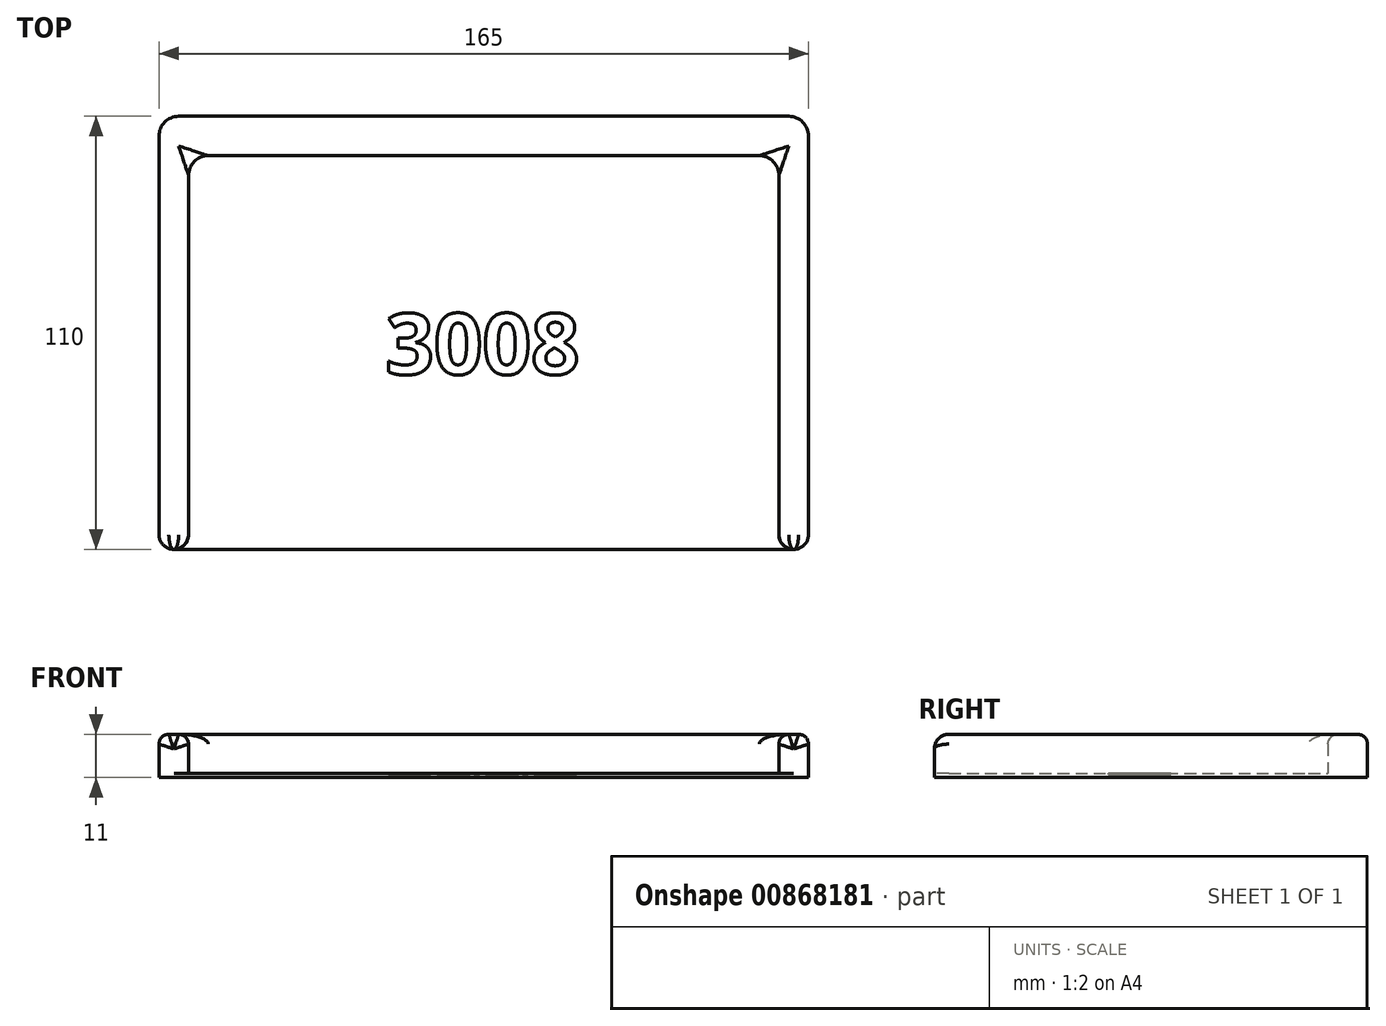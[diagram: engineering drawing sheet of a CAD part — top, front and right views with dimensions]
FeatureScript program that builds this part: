
annotation { "Feature Type Name" : "Feature", "Feature Type Description" : "" }
export const myFeature = defineFeature(function(context is Context, id is Id, definition is map)
    precondition{}
    {
        {
            var Q0;
            Q0=qCreatedBy(makeId("Top.planeOp"),FACE);
            var sketch = newSketch(context, id + "F0", { "sketchPlane" : qUnion([Q0])});
            skLineSegment(sketch, "E0.bottom", {"start": v(0, 0) * mm, "end": v(165, 0) * mm});
            skLineSegment(sketch, "E0.top", {"start": v(0, 110) * mm, "end": v(165, 110) * mm});
            skLineSegment(sketch, "E0.left", {"start": v(0, 0) * mm, "end": v(0, 110) * mm});
            skLineSegment(sketch, "E0.right", {"start": v(165, 0) * mm, "end": v(165, 110) * mm});
            skSolve(sketch);
        }
        {
            var Q0;
            Q0 = qSketchRegion(id + "F0", true);
            extrude(context, id + "F1", {"entities" : qUnion([Q0]), "depth" : 1 * mm, "offsetDistance" : 25 * mm});
        }
        {
            var Q0;
            Q0=makeQuery(id+"F1.opExtrude","CAP_FACE",FACE,{"disambiguationData":[OSD([sQuery(id+"F0.wireOp",EDGE,"E0.bottom"),sQuery(id+"F0.wireOp",EDGE,"E0.top"),sQuery(id+"F0.wireOp",EDGE,"E0.left"),sQuery(id+"F0.wireOp",EDGE,"E0.right")])],"isStart":false});
            var sketch = newSketch(context, id + "F2", { "sketchPlane" : qUnion([Q0])});
            skLineSegment(sketch, "E1", {"start": v(0, 0) * mm, "end": v(0, 110) * mm});
            skLineSegment(sketch, "E2", {"start": v(0, 110) * mm, "end": v(165, 110) * mm});
            skLineSegment(sketch, "E3", {"start": v(165, 110) * mm, "end": v(165, 0) * mm});
            skLineSegment(sketch, "E4", {"start": v(165, 0) * mm, "end": v(157.5, 0) * mm});
            skLineSegment(sketch, "E5", {"start": v(157.5, 0) * mm, "end": v(157.5, 100) * mm});
            skLineSegment(sketch, "E6", {"start": v(157.5, 100) * mm, "end": v(7.5, 100) * mm});
            skLineSegment(sketch, "E7", {"start": v(7.5, 100) * mm, "end": v(7.5, 0) * mm});
            skLineSegment(sketch, "E8", {"start": v(7.5, 0) * mm, "end": v(0, 0) * mm});
            skSolve(sketch);
        }
        {
            var Q0;
            Q0 = qSketchRegion(id + "F2", true);
            extrude(context, id + "F3", {"entities" : qUnion([Q0]), "operationType" : NewBodyOperationType.ADD, "depth" : 10 * mm, "offsetDistance" : 25 * mm});
        }
        {
            var Q0;
            Q0=makeQuery(id+"F3.opExtrude","CAP_EDGE",EDGE,{"disambiguationData":[OSD([sQuery(id+"F2.wireOp",EDGE,"E7")])],"isStart":false});
            var Q1;
            Q1=makeQuery(id+"F3.opExtrude","CAP_EDGE",EDGE,{"disambiguationData":[OSD([sQuery(id+"F2.wireOp",EDGE,"E6")])],"isStart":false});
            var Q2;
            Q2=makeQuery(id+"F3.opExtrude","CAP_EDGE",EDGE,{"disambiguationData":[OSD([sQuery(id+"F2.wireOp",EDGE,"E5")])],"isStart":false});
            var Q3;
            Q3=makeQuery(id+"F3.opExtrude","CAP_EDGE",EDGE,{"disambiguationData":[OSD([sQuery(id+"F2.wireOp",EDGE,"E1")])],"isStart":false});
            var Q4;
            Q4=makeQuery(id+"F3.opExtrude","CAP_EDGE",EDGE,{"disambiguationData":[OSD([sQuery(id+"F2.wireOp",EDGE,"E2")])],"isStart":false});
            var Q5;
            Q5=makeQuery(id+"F3.opExtrude","CAP_EDGE",EDGE,{"disambiguationData":[OSD([sQuery(id+"F2.wireOp",EDGE,"E3")])],"isStart":false});
            fillet(context, id + "F4", {"entities" : qUnion([Q0, Q1, Q2, Q3, Q4, Q5]), "radius" : 2.5 * mm, "tangentPropagation" : true, "allowEdgeOverflow" : false});
        }
        {
            var Q0;
            Q0=makeQuery(id+"F1.opExtrude","CAP_FACE",FACE,{"disambiguationData":[OSD([sQuery(id+"F0.wireOp",EDGE,"E0.bottom"),sQuery(id+"F0.wireOp",EDGE,"E0.top"),sQuery(id+"F0.wireOp",EDGE,"E0.left"),sQuery(id+"F0.wireOp",EDGE,"E0.right")])],"isStart":false});
            var sketch = newSketch(context, id + "F5", { "sketchPlane" : qUnion([Q0])});
            skText(sketch, "E9", { "text": "3008", "fontName": "OpenSans-Bold.ttf"});
            const initialGuessF5  = {"E9": [0.0575, 0.04444, 1, 0, 0.01556]};
            skSetInitialGuess(sketch, initialGuessF5);
            skSolve(sketch);
        }
        {
            var Q0;
            Q0 = qSketchRegion(id + "F5", true);
            extrude(context, id + "F6", {"entities" : qUnion([Q0]), "operationType" : NewBodyOperationType.REMOVE, "oppositeDirection" : true, "depth" : .2 * mm, "offsetDistance" : 25 * mm});
        }
        {
            var Q0;
            Q0=makeQuery(id+"F3.opExtrude","SWEPT_EDGE",EDGE,{"disambiguationData":[OSD([sQuery(id+"F2.wireOp",EDGE,"E6"),sQuery(id+"F2.wireOp",EDGE,"E7")])]});
            var Q1;
            Q1=makeQuery(id+"F3.boolean.opBoolean","MERGE",EDGE,{"derivedFrom":[makeQuery(id+"F1.opExtrude","SWEPT_EDGE",EDGE,{"disambiguationData":[OSD([sQuery(id+"F0.wireOp",EDGE,"E0.top"),sQuery(id+"F0.wireOp",EDGE,"E0.left")])]}),makeQuery(id+"F3.opExtrude","SWEPT_EDGE",EDGE,{"disambiguationData":[OSD([sQuery(id+"F2.wireOp",EDGE,"E1"),sQuery(id+"F2.wireOp",EDGE,"E2")])]})]});
            var Q2;
            Q2=makeQuery(id+"F3.opExtrude","SWEPT_EDGE",EDGE,{"disambiguationData":[OSD([sQuery(id+"F2.wireOp",EDGE,"E5"),sQuery(id+"F2.wireOp",EDGE,"E6")])]});
            var Q3;
            Q3=makeQuery(id+"F3.boolean.opBoolean","MERGE",EDGE,{"derivedFrom":[makeQuery(id+"F1.opExtrude","SWEPT_EDGE",EDGE,{"disambiguationData":[OSD([sQuery(id+"F0.wireOp",EDGE,"E0.top"),sQuery(id+"F0.wireOp",EDGE,"E0.right")])]}),makeQuery(id+"F3.opExtrude","SWEPT_EDGE",EDGE,{"disambiguationData":[OSD([sQuery(id+"F2.wireOp",EDGE,"E2"),sQuery(id+"F2.wireOp",EDGE,"E3")])]})]});
            fillet(context, id + "F7", {"entities" : qUnion([Q0, Q1, Q2, Q3]), "radius" : 5 * mm, "tangentPropagation" : true, "allowEdgeOverflow" : false});
        }
        {
            var Q0;
            Q0=makeQuery(id+"F3.opExtrude","SWEPT_EDGE",EDGE,{"disambiguationData":[OSD([sQuery(id+"F0.wireOp",EDGE,"E0.bottom"),sQuery(id+"F2.wireOp",EDGE,"E7"),sQuery(id+"F2.wireOp",EDGE,"E8")])]});
            var Q1;
            Q1=makeQuery(id+"F3.boolean.opBoolean","MERGE",EDGE,{"derivedFrom":[makeQuery(id+"F1.opExtrude","SWEPT_EDGE",EDGE,{"disambiguationData":[OSD([sQuery(id+"F0.wireOp",EDGE,"E0.bottom"),sQuery(id+"F0.wireOp",EDGE,"E0.left")])]}),makeQuery(id+"F3.opExtrude","SWEPT_EDGE",EDGE,{"disambiguationData":[OSD([sQuery(id+"F2.wireOp",EDGE,"E1"),sQuery(id+"F2.wireOp",EDGE,"E8")])]})]});
            var Q2;
            Q2=makeQuery(id+"F3.opExtrude","SWEPT_EDGE",EDGE,{"disambiguationData":[OSD([sQuery(id+"F0.wireOp",EDGE,"E0.bottom"),sQuery(id+"F2.wireOp",EDGE,"E4"),sQuery(id+"F2.wireOp",EDGE,"E5")])]});
            var Q3;
            Q3=makeQuery(id+"F3.boolean.opBoolean","MERGE",EDGE,{"derivedFrom":[makeQuery(id+"F1.opExtrude","SWEPT_EDGE",EDGE,{"disambiguationData":[OSD([sQuery(id+"F0.wireOp",EDGE,"E0.bottom"),sQuery(id+"F0.wireOp",EDGE,"E0.right")])]}),makeQuery(id+"F3.opExtrude","SWEPT_EDGE",EDGE,{"disambiguationData":[OSD([sQuery(id+"F2.wireOp",EDGE,"E3"),sQuery(id+"F2.wireOp",EDGE,"E4")])]})]});
            fillet(context, id + "F8", {"entities" : qUnion([Q0, Q1, Q2, Q3]), "radius" : 3.7 * mm, "tangentPropagation" : true, "allowEdgeOverflow" : false});
        }
    });
